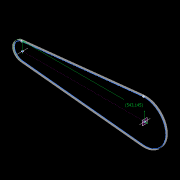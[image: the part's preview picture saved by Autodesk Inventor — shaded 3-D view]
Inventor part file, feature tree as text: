
AUTODESK INVENTOR PART (.ipt)
format: ipt  version: 2021 (Build 250183000, 183)  size: 130,560 bytes
history: native  units: mm
features: other x63, plane x3, pattern_linear x3, sketch x2, extrude x1
ambient origin geometry x8: Origin, YZ Plane, XZ Plane, XY Plane, X Axis, Y Axis, Z Axis, Center Point
bodies: Solid1 (feature_tree), Solid (feature_tree)
feature tree (72):
  other  "Work Axis1"
  other  "Work Axis2"
  plane  "Work Plane2"
  plane  "Work Plane3"
  other  "Path"
  other  "Section Plane"
  pattern_linear  "Strand Pattern"  Spacing1=3.66mm  [1 undecoded]
  other  "Work Point10"
  other  "Work Point11"
  other  "Work Point12"
  sketch  "Sketch5"  dims[d4=0.0mm d21=3.66mm d22=7.75mm d23=3.3mm d24=2.0mm d28=10.0mm d30=13.92mm d31=9.91mm d32=10.2mm d33=0.0mm d34=0.0mm d35=0.0mm d36=0.0mm d37=0.0mm d38=3.875mm d39=10.0mm d40=0.0mm d42=543.145102mm d43=20.0mm d45=543.145102mm d46=0.0mm d47=540.0mm]
  pattern_linear  "Rectangular Pattern5"  Spacing1=7.75mm  [1 undecoded]
  plane  "Work Plane7"
  pattern_linear  "Rectangular Pattern6"  Spacing1=3.3mm  [1 undecoded]
  other  "Section Sketch"
  sketch  "Sketch4"  dims[d2=0.0mm]
  other  "Srf1"
  other  "Work Point13"
  other  "Work Point14"
  other  "Work Point15"
  other  "Work Point16"
  other  "Work Point17"
  other  "Work Point18"
  other  "Work Point19"
  other  "Work Point20"
  other  "Work Point21"
  other  "Work Point22"
  other  "Work Point23"
  other  "Work Point24"
  other  "Work Point25"
  other  "Work Point26"
  other  "Work Point27"
  other  "Work Point28"
  other  "Work Point29"
  other  "Work Point30"
  other  "Work Point31"
  other  "Work Point32"
  other  "Work Point33"
  other  "Work Point34"
  other  "Work Point35"
  other  "Work Point36"
  other  "Work Point37"
  other  "Work Point38"
  other  "Work Point39"
  other  "Work Point40"
  other  "Work Point41"
  other  "Work Point42"
  other  "Work Point43"
  other  "Work Point44"
  other  "Work Point45"
  other  "Work Point46"
  other  "Work Point47"
  other  "Work Point48"
  other  "Work Point49"
  other  "Work Point50"
  other  "Work Point51"
  other  "Work Point52"
  other  "Work Point53"
  other  "Work Point54"
  other  "Work Point55"
  other  "Work Point56"
  other  "Work Point57"
  other  "Work Point58"
  other  "Work Point59"
  other  "Work Point60"
  other  "Work Point61"
  other  "Work Point62"
  other  "Work Point63"
  other  "Work Point64"
  other  "Work Point65"
  other  "Work Point66"
  extrude  "ExtrusionSrf1"  Depth=543.145102mm
note: 3 required parameter values undecoded (feature->parameter linkage not recoverable at this tier; creation-order binding heuristic only, values carry confidence <= 0.55)
